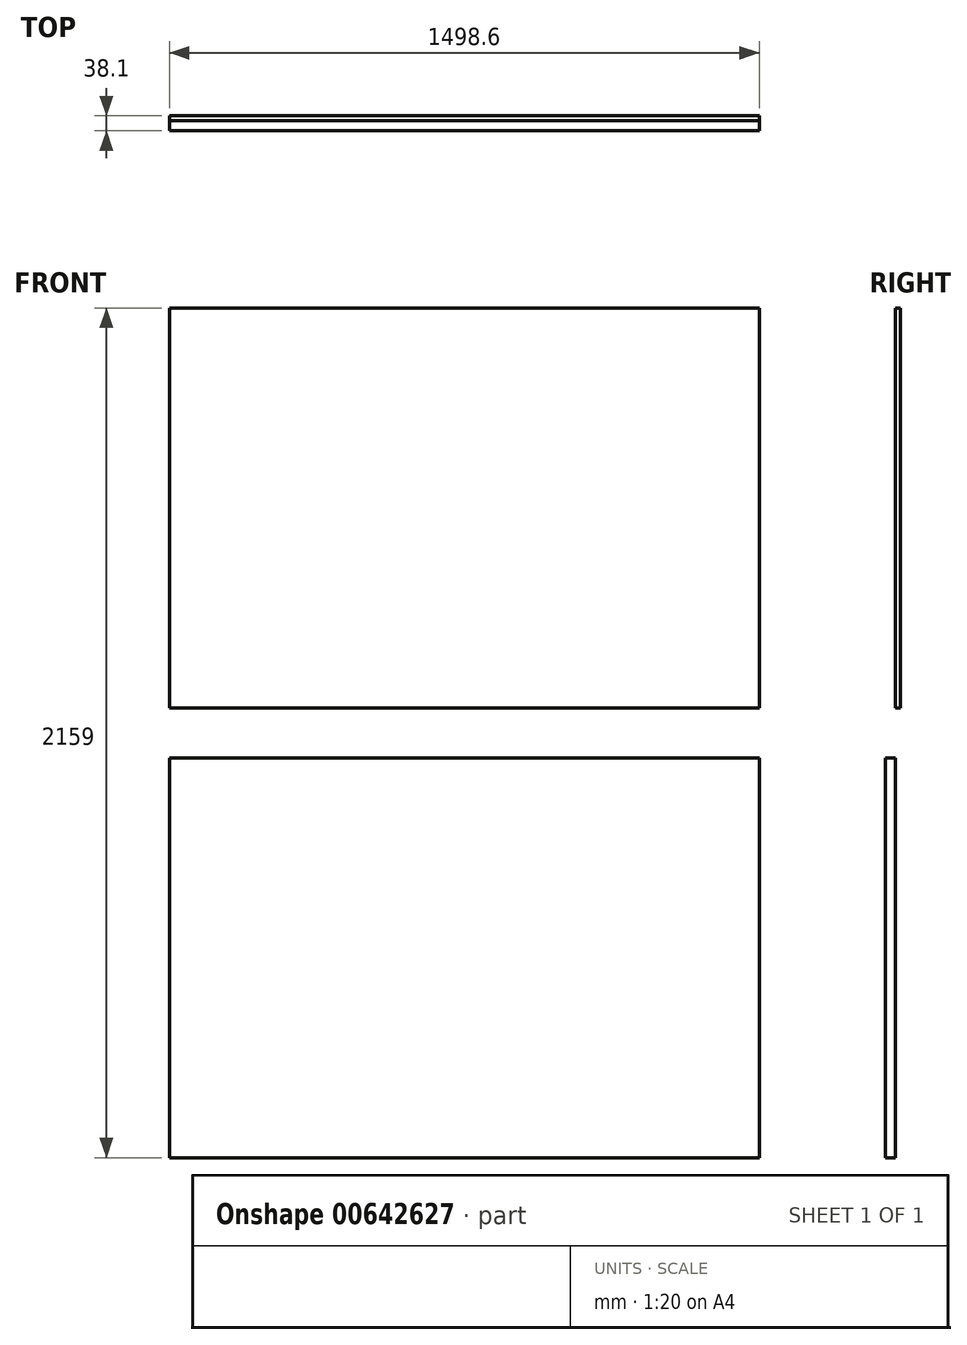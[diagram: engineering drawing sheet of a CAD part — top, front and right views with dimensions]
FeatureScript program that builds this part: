
annotation { "Feature Type Name" : "Feature", "Feature Type Description" : "" }
export const myFeature = defineFeature(function(context is Context, id is Id, definition is map)
    precondition{}
    {
        {
            var Q0;
            Q0=qCreatedBy(makeId("Front.planeOp"),FACE);
            var sketch = newSketch(context, id + "F0", { "sketchPlane" : qUnion([Q0])});
            skLineSegment(sketch, "E0.bottom", {"start": v(749.3, 508) * mm, "end": v(-749.3, 508) * mm});
            skLineSegment(sketch, "E0.top", {"start": v(749.3, -508) * mm, "end": v(-749.3, -508) * mm});
            skLineSegment(sketch, "E0.left", {"start": v(749.3, 508) * mm, "end": v(749.3, -508) * mm});
            skLineSegment(sketch, "E0.right", {"start": v(-749.3, 508) * mm, "end": v(-749.3, -508) * mm});
            skPoint(sketch, "E0.middle", {"position": v(0, 0) * mm});
            skSolve(sketch);
        }
        {
            var Q0;
            Q0=makeQuery(id+"F0.imprint","IMPRINT",FACE,{"disambiguationData":[TD([[makeQuery(id+"F0.imprint","IMPRINT",EDGE,{"derivedFrom":sQuery(id+"F0.wireOp",EDGE,"E0.bottom")}),1.0]])]});
            extrude(context, id + "F1", {"entities" : qUnion([Q0]), "depth" : 12.7 * mm, "offsetDistance" : 25 * mm});
        }
        {
            var Q0;
            Q0=makeQuery(id+"F1.opExtrude","CAP_FACE",FACE,{"disambiguationData":[OSD([sQuery(id+"F0.wireOp",EDGE,"E0.bottom"),sQuery(id+"F0.wireOp",EDGE,"E0.top"),sQuery(id+"F0.wireOp",EDGE,"E0.left"),sQuery(id+"F0.wireOp",EDGE,"E0.right")])],"isStart":false});
            var sketch = newSketch(context, id + "F2", { "sketchPlane" : qUnion([Q0])});
            skLineSegment(sketch, "E1.bottom", {"start": v(-749.3, -635) * mm, "end": v(749.3, -635) * mm});
            skLineSegment(sketch, "E1.top", {"start": v(-749.3, -1651) * mm, "end": v(749.3, -1651) * mm});
            skLineSegment(sketch, "E1.left", {"start": v(-749.3, -635) * mm, "end": v(-749.3, -1651) * mm});
            skLineSegment(sketch, "E1.right", {"start": v(749.3, -635) * mm, "end": v(749.3, -1651) * mm});
            skSolve(sketch);
        }
        {
            var Q0;
            Q0=makeQuery(id+"F2.imprint","IMPRINT",FACE,{"disambiguationData":[TD([[makeQuery(id+"F2.imprint","IMPRINT",EDGE,{"derivedFrom":sQuery(id+"F2.wireOp",EDGE,"E1.bottom")}),-1.0]])]});
            extrude(context, id + "F3", {"entities" : qUnion([Q0]), "depth" : 25.4 * mm, "offsetDistance" : 25.4 * mm});
        }
    });
